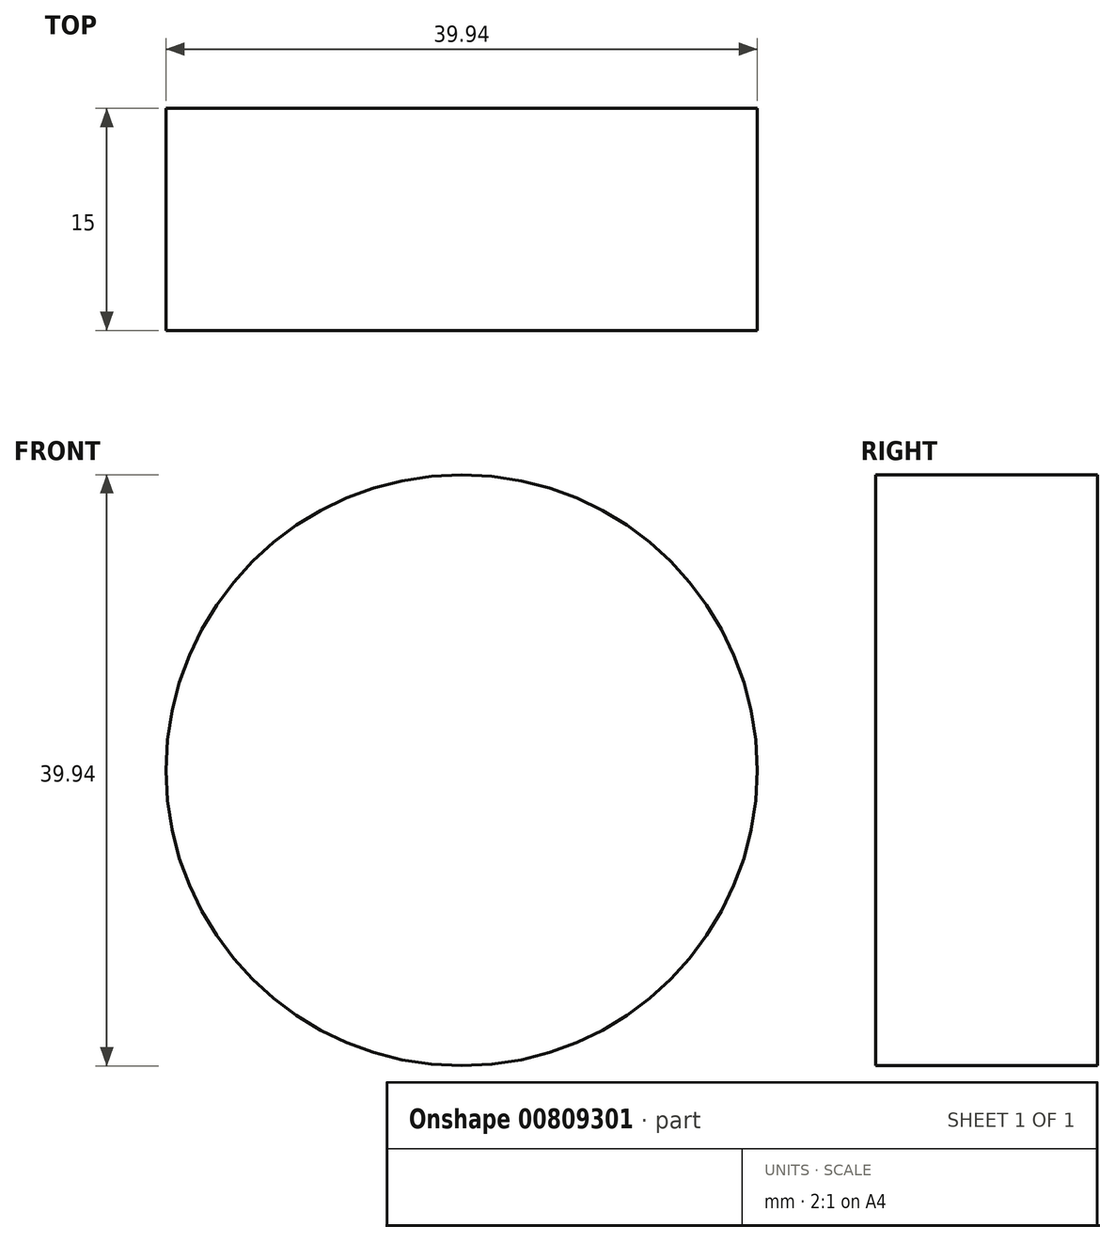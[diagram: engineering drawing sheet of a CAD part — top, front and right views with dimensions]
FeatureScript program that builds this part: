
annotation { "Feature Type Name" : "Feature", "Feature Type Description" : "" }
export const myFeature = defineFeature(function(context is Context, id is Id, definition is map)
    precondition{}
    {
        {
            var Q0;
            Q0=qCreatedBy(makeId("Front.planeOp"),FACE);
            var sketch = newSketch(context, id + "F0", { "sketchPlane" : qUnion([Q0])});
            skCircle(sketch, "E0", {"center": v(0, 0) * mm, "radius": 19.97 * mm});
            skSolve(sketch);
        }
        {
            var Q0;
            Q0=makeQuery(id+"F0.imprint","IMPRINT",FACE,{"disambiguationData":[TD([[makeQuery(id+"F0.imprint","IMPRINT",EDGE,{"derivedFrom":sQuery(id+"F0.wireOp",EDGE,"E0")}),1.0]])]});
            extrude(context, id + "F1", {"entities" : qUnion([Q0]), "depth" : 15 * mm, "offsetDistance" : 25 * mm});
        }
    });
